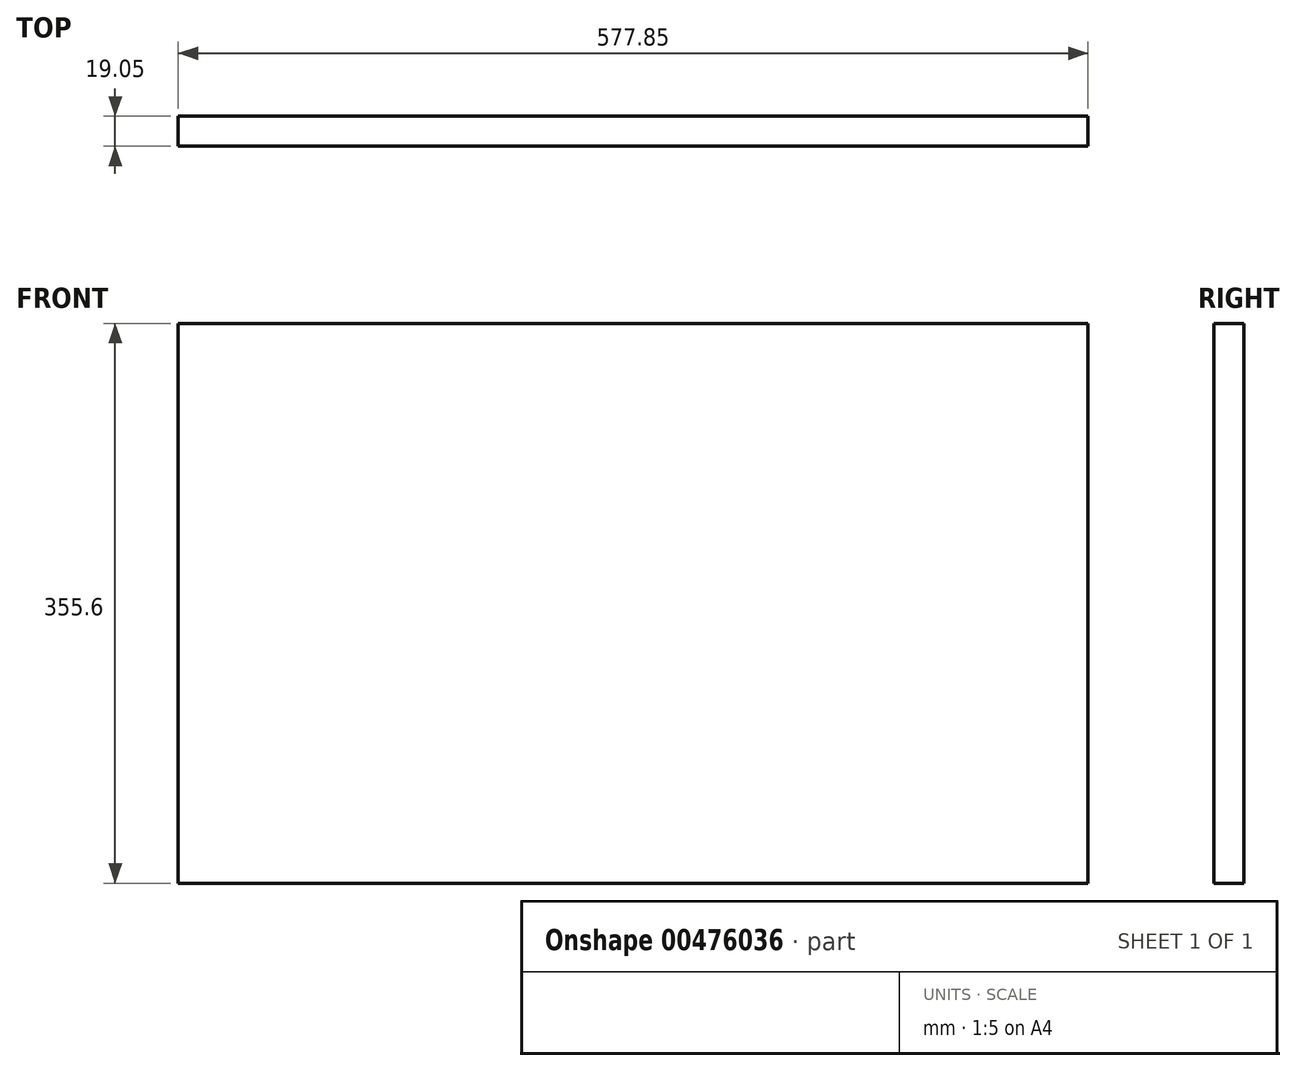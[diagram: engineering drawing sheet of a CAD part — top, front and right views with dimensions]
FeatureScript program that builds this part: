
annotation { "Feature Type Name" : "Feature", "Feature Type Description" : "" }
export const myFeature = defineFeature(function(context is Context, id is Id, definition is map)
    precondition{}
    {
        {
            var Q0;
            Q0=qCreatedBy(makeId("Front.planeOp"),FACE);
            var sketch = newSketch(context, id + "F0", { "sketchPlane" : qUnion([Q0])});
            skLineSegment(sketch, "E0.bottom", {"start": v(0, 0) * mm, "end": v(577.85, 0) * mm});
            skLineSegment(sketch, "E0.top", {"start": v(0, 355.6) * mm, "end": v(577.85, 355.6) * mm});
            skLineSegment(sketch, "E0.left", {"start": v(0, 0) * mm, "end": v(0, 355.6) * mm});
            skLineSegment(sketch, "E0.right", {"start": v(577.85, 0) * mm, "end": v(577.85, 355.6) * mm});
            skLineSegment(sketch, "E1.bottom", {"start": v(-114.75, 270.48) * mm, "end": v(-684.4, 270.48) * mm});
            skLineSegment(sketch, "E1.top", {"start": v(-114.75, 114.75) * mm, "end": v(-684.4, 114.75) * mm});
            skLineSegment(sketch, "E1.left", {"start": v(-114.75, 270.48) * mm, "end": v(-114.75, 114.75) * mm});
            skLineSegment(sketch, "E1.right", {"start": v(-684.4, 270.48) * mm, "end": v(-684.4, 114.75) * mm});
            skSolve(sketch);
        }
        {
            var Q0;
            Q0=makeQuery(id+"F0.imprint","IMPRINT",FACE,{"disambiguationData":[TD([[makeQuery(id+"F0.imprint","IMPRINT",EDGE,{"derivedFrom":sQuery(id+"F0.wireOp",EDGE,"E0.bottom")}),1.0]])]});
            extrude(context, id + "F1", {"entities" : qUnion([Q0]), "depth" : 19.05 * mm});
        }
    });
